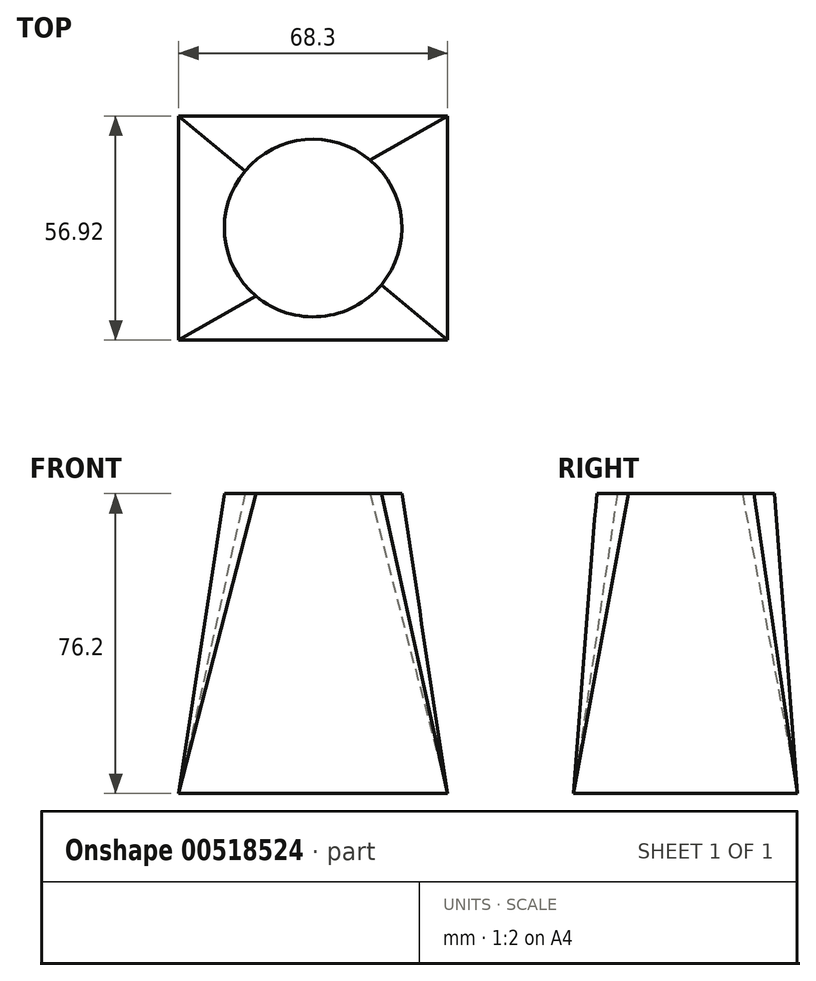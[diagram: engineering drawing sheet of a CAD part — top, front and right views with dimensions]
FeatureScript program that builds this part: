
annotation { "Feature Type Name" : "Feature", "Feature Type Description" : "" }
export const myFeature = defineFeature(function(context is Context, id is Id, definition is map)
    precondition{}
    {
        {
            var Q0;
            Q0=qCreatedBy(makeId("Top.planeOp"),FACE);
            var sketch = newSketch(context, id + "F0", { "sketchPlane" : qUnion([Q0])});
            skLineSegment(sketch, "E0.bottom", {"start": v(34.15, -28.46) * mm, "end": v(-34.15, -28.46) * mm});
            skLineSegment(sketch, "E0.top", {"start": v(34.15, 28.46) * mm, "end": v(-34.15, 28.46) * mm});
            skLineSegment(sketch, "E0.left", {"start": v(34.15, -28.46) * mm, "end": v(34.15, 28.46) * mm});
            skLineSegment(sketch, "E0.right", {"start": v(-34.15, -28.46) * mm, "end": v(-34.15, 28.46) * mm});
            skPoint(sketch, "E0.middle", {"position": v(0, 0) * mm});
            skSolve(sketch);
        }
        {
            var Q0;
            Q0=qCreatedBy(makeId("Top.planeOp"),FACE);
            cPlane(context, id + "F1", {"entities" : qUnion([Q0]), "cplaneType" : CPlaneType.OFFSET, "offset" : 76.2 * mm, "width" : 152.4 * mm, "height" : 152.4 * mm});
        }
        {
            var Q0;
            Q0=qCreatedBy(id+"F1.planeOp",FACE);
            var sketch = newSketch(context, id + "F2", { "sketchPlane" : qUnion([Q0])});
            skCircle(sketch, "E1", {"center": v(0, 0) * mm, "radius": 22.56 * mm});
            skSolve(sketch);
        }
        {
            var Q0;
            Q0=makeQuery(id+"F2.imprint","IMPRINT",FACE,{"disambiguationData":[TD([[makeQuery(id+"F2.imprint","IMPRINT",EDGE,{"derivedFrom":sQuery(id+"F2.wireOp",EDGE,"E1")}),1.0]])]});
            var Q1;
            Q1=makeQuery(id+"F0.imprint","IMPRINT",FACE,{"disambiguationData":[TD([[makeQuery(id+"F0.imprint","IMPRINT",EDGE,{"derivedFrom":sQuery(id+"F0.wireOp",EDGE,"E0.bottom")}),-1.0]])]});
            loft(context, id + "F3", {"sheetProfilesArray" : [{ "sheetProfileEntities" : qUnion([Q0]) }, { "sheetProfileEntities" : qUnion([Q1]) }]});
        }
    });
